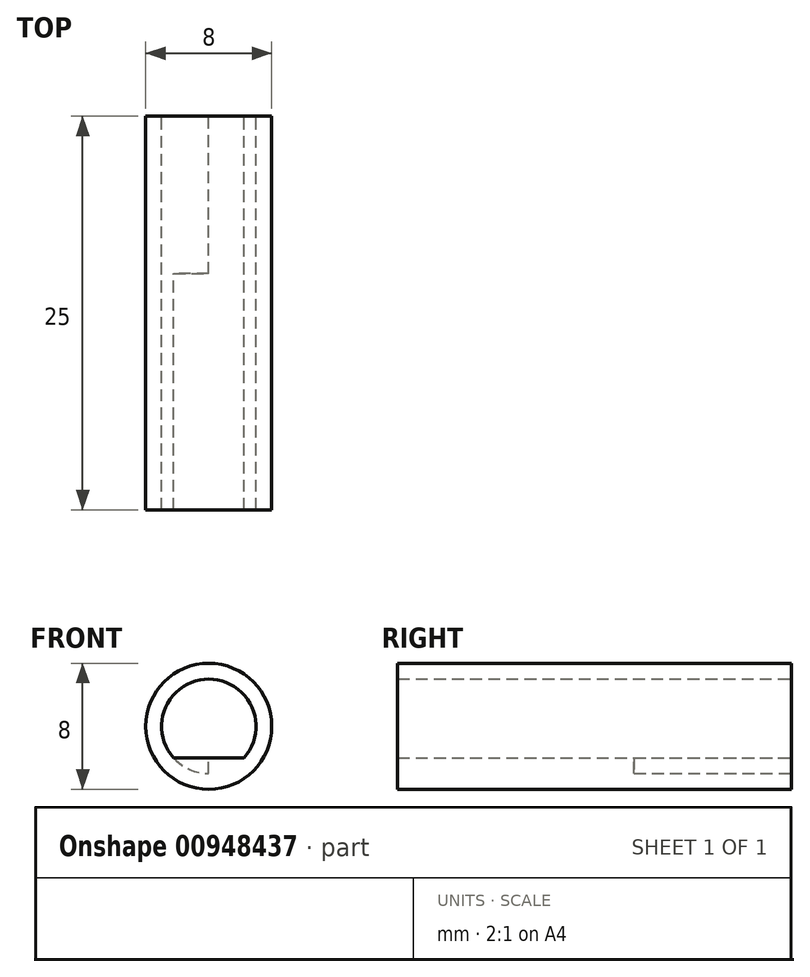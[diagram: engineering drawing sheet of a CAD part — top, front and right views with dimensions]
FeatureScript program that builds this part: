
annotation { "Feature Type Name" : "Feature", "Feature Type Description" : "" }
export const myFeature = defineFeature(function(context is Context, id is Id, definition is map)
    precondition{}
    {
        {
            var Q0;
            Q0=qCreatedBy(makeId("Front.planeOp"),FACE);
            var sketch = newSketch(context, id + "F0", { "sketchPlane" : qUnion([Q0])});
            skCircle(sketch, "E0", {"center": v(0, 0) * mm, "radius": 4 * mm});
            skCircle(sketch, "E1", {"center": v(0, 0) * mm, "radius": 3 * mm});
            skLineSegment(sketch, "E2", {"start": v(0, -3) * mm, "end": v(0, -2) * mm});
            skLineSegment(sketch, "E3", {"start": v(0, -2) * mm, "end": v(2.24, -2) * mm});
            skLineSegment(sketch, "E4", {"start": v(2.24, -2) * mm, "end": v(-2.24, -2) * mm});
            skSolve(sketch);
        }
        {
            var Q0;
            {var subQ0=sQuery(id+"F0.wireOp",EDGE,"E4");var subQ1=sQuery(id+"F0.wireOp",EDGE,"E1");var subQ2=makeQuery(id+"F0.imprint","INTERSECT",VERTEX,{"disambiguationData":[OD(0.0)],"derivedFrom":[subQ1,subQ0]});Q0=makeQuery(id+"F0.imprint","IMPRINT",FACE,{"disambiguationData":[TD([[makeQuery(id+"F0.imprint","IMPRINT",EDGE,{"disambiguationData":[TD([[subQ2,-1.0]])],"derivedFrom":subQ1}),1.0]])]});}
            var Q1;
            {var subQ0=sQuery(id+"F0.wireOp",EDGE,"E2");Q1=makeQuery(id+"F0.imprint","IMPRINT",FACE,{"disambiguationData":[TD([[makeQuery(id+"F0.imprint","IMPRINT",EDGE,{"derivedFrom":subQ0}),-1.0]])]});}
            var Q2;
            {var subQ0=sQuery(id+"F0.wireOp",EDGE,"E2");Q2=makeQuery(id+"F0.imprint","IMPRINT",FACE,{"disambiguationData":[TD([[makeQuery(id+"F0.imprint","IMPRINT",EDGE,{"derivedFrom":subQ0}),1.0]])]});}
            var Q3;
            Q3=makeQuery(id+"F0.imprint","IMPRINT",FACE,{"disambiguationData":[TD([[makeQuery(id+"F0.imprint","IMPRINT",EDGE,{"derivedFrom":sQuery(id+"F0.wireOp",EDGE,"E0")}),1.0]])]});
            extrude(context, id + "F1", {"entities" : qUnion([Q0, Q1, Q2, Q3]), "depth" : 25 * mm, "offsetDistance" : 25 * mm});
        }
        {
            var Q0;
            {var subQ0=sQuery(id+"F0.wireOp",EDGE,"E4");var subQ1=sQuery(id+"F0.wireOp",EDGE,"E1");var subQ2=makeQuery(id+"F0.imprint","INTERSECT",VERTEX,{"disambiguationData":[OD(0.0)],"derivedFrom":[subQ1,subQ0]});Q0=makeQuery(id+"F0.imprint","IMPRINT",FACE,{"disambiguationData":[TD([[makeQuery(id+"F0.imprint","IMPRINT",EDGE,{"disambiguationData":[TD([[subQ2,-1.0]])],"derivedFrom":subQ1}),1.0]])]});}
            extrude(context, id + "F2", {"entities" : qUnion([Q0]), "operationType" : NewBodyOperationType.REMOVE, "depth" : 10 * mm, "offsetDistance" : 25 * mm});
        }
    });
